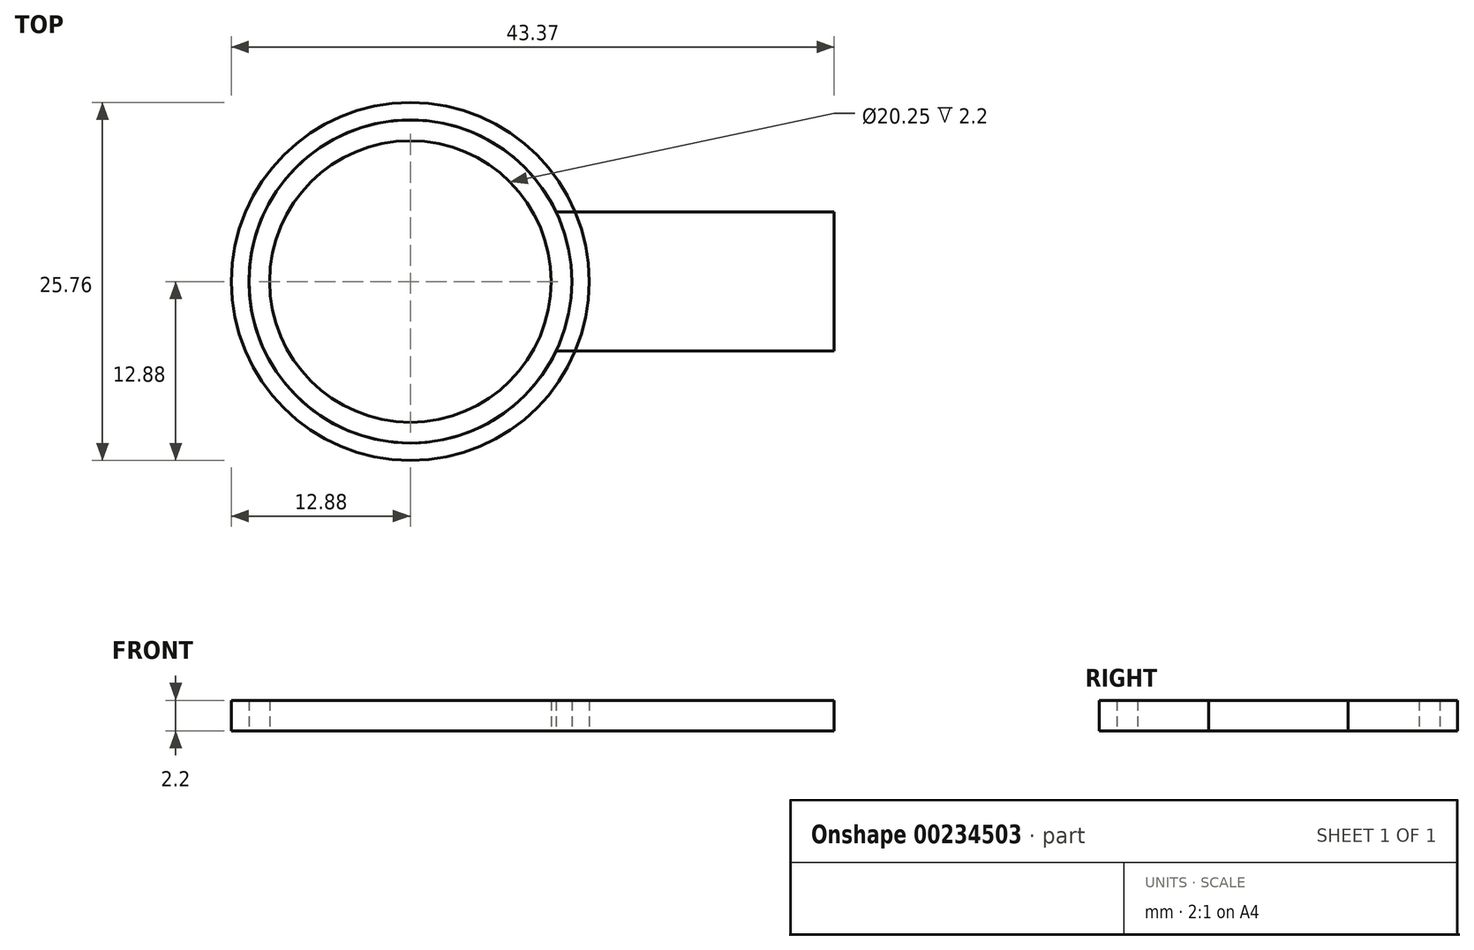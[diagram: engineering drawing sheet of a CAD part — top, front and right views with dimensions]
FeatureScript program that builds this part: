
annotation { "Feature Type Name" : "Feature", "Feature Type Description" : "" }
export const myFeature = defineFeature(function(context is Context, id is Id, definition is map)
    precondition{}
    {
        {
            var Q0;
            Q0=qCreatedBy(makeId("Top.planeOp"),FACE);
            var sketch = newSketch(context, id + "F0", { "sketchPlane" : qUnion([Q0])});
            skCircle(sketch, "E0", {"center": v(0, 0) * mm, "radius": 12.88 * mm});
            skSolve(sketch);
        }
        {
            var Q0;
            Q0 = qSketchRegion(id + "F0", true);
            extrude(context, id + "F1", {"entities" : qUnion([Q0]), "depth" : 2.2 * mm});
        }
        {
            var Q0;
            Q0=qCreatedBy(makeId("Top.planeOp"),FACE);
            var sketch = newSketch(context, id + "F2", { "sketchPlane" : qUnion([Q0])});
            skCircle(sketch, "E1", {"center": v(0, 0) * mm, "radius": 11.62 * mm});
            skSolve(sketch);
        }
        {
            var Q0;
            Q0 = qSketchRegion(id + "F2", true);
            extrude(context, id + "F3", {"entities" : qUnion([Q0]), "depth" : 2.2 * mm});
        }
        {
            var Q0;
            Q0=qCreatedBy(makeId("Top.planeOp"),FACE);
            var sketch = newSketch(context, id + "F4", { "sketchPlane" : qUnion([Q0])});
            skArc(sketch, "E2", {"start": v(10.5, 5) * mm, "mid": v(-11.63, 0) * mm, "end": v(10.5, -5) * mm});
            skLineSegment(sketch, "E3.bottom", {"start": v(10.5, 5) * mm, "end": v(30.5, 5) * mm});
            skLineSegment(sketch, "E3.top", {"start": v(10.5, -5) * mm, "end": v(30.5, -5) * mm});
            skLineSegment(sketch, "E3.right", {"start": v(30.5, 5) * mm, "end": v(30.5, -5) * mm});
            skCircle(sketch, "E4.0", {"center": v(0, 0) * mm, "radius": 10.13 * mm});
            skSolve(sketch);
        }
        {
            var Q0;
            Q0 = qSketchRegion(id + "F4", true);
            extrude(context, id + "F5", {"entities" : qUnion([Q0]), "depth" : 2.2 * mm});
        }
    });
